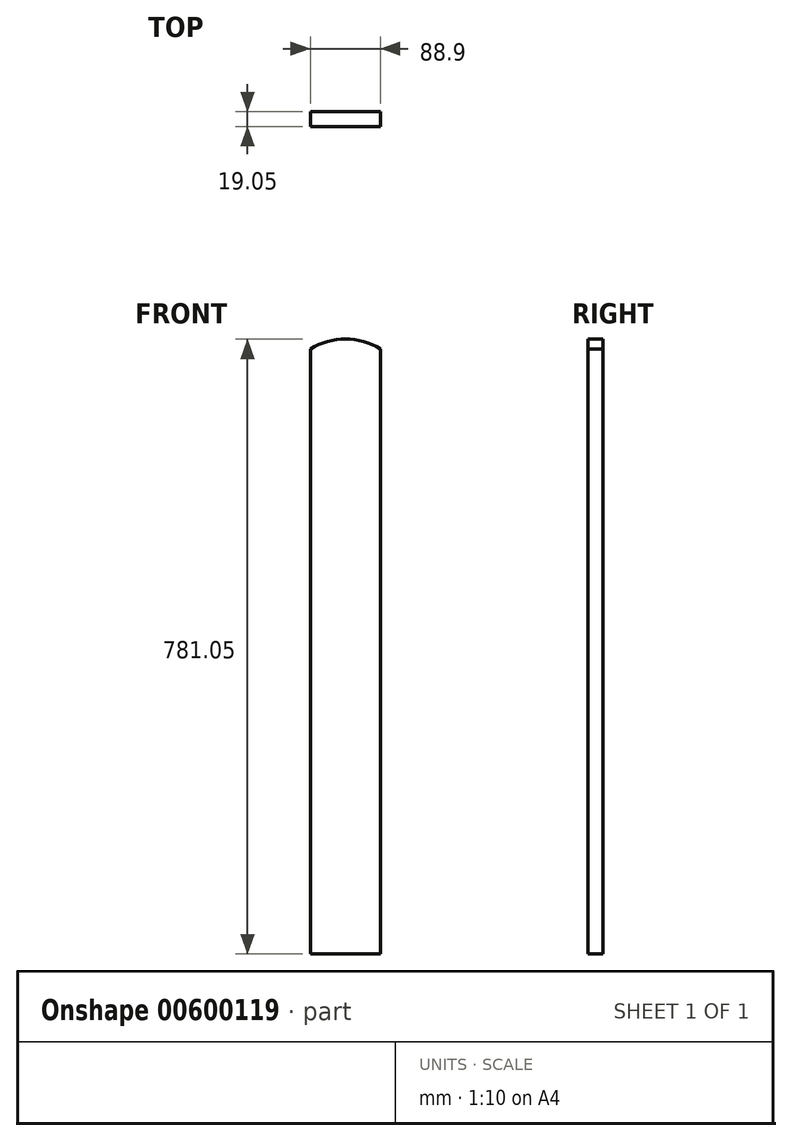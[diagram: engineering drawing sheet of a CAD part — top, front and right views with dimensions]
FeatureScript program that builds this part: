
annotation { "Feature Type Name" : "Feature", "Feature Type Description" : "" }
export const myFeature = defineFeature(function(context is Context, id is Id, definition is map)
    precondition{}
    {
        {
            var Q0;
            Q0=qCreatedBy(makeId("Front.planeOp"),FACE);
            var sketch = newSketch(context, id + "F0", { "sketchPlane" : qUnion([Q0])});
            skLineSegment(sketch, "E0.bottom", {"start": v(0, 0) * mm, "end": v(-88.9, 0) * mm});
            skLineSegment(sketch, "E0.top", {"start": v(0, 768.35) * mm, "end": v(-88.9, 768.35) * mm, "construction": true});
            skLineSegment(sketch, "E0.left", {"start": v(0, 0) * mm, "end": v(0, 768.35) * mm});
            skLineSegment(sketch, "E0.right", {"start": v(-88.9, 0) * mm, "end": v(-88.9, 768.35) * mm});
            skArc(sketch, "E1", {"start": v(0, 768.35) * mm, "mid": v(-44.45, 781.05) * mm, "end": v(-88.9, 768.35) * mm});
            skLineSegment(sketch, "E2", {"start": v(-44.45, 781.05) * mm, "end": v(-44.45, 768.35) * mm, "construction": true});
            skSolve(sketch);
        }
        {
            var Q0;
            Q0 = qSketchRegion(id + "F0", true);
            extrude(context, id + "F1", {"entities" : qUnion([Q0]), "depth" : 19.05 * mm, "offsetDistance" : 25.4 * mm});
        }
    });
